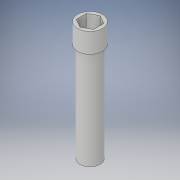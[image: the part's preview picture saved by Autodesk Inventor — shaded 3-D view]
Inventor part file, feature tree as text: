
AUTODESK INVENTOR PART (.ipt)
format: ipt  version: 2018 (Build 220112000, 112)  size: 112,640 bytes
history: native  units: in
note: dims shown in document units (in); Inventor stores cm internally (conversion verified against a paired STEP export)
features: extrude x3, sketch x3
ambient origin geometry x8: Origin, YZ Plane, XZ Plane, XY Plane, X Axis, Y Axis, Z Axis, Center Point
bodies: Solid1 (feature_tree)
feature tree (6):
  extrude  "Extrusion1"  Depth=1.0in TaperAngle=0.0deg
  extrude  "Extrusion2"  Depth=0.2in TaperAngle=0.0deg
  extrude  "Extrusion3"  [1 undecoded]
  sketch  "Sketch1"  dims[d0=0.2031in d1=1.0in d2=0.0in]
  sketch  "Sketch2"  dims[d3=0.25in d4=0.2in d5=0.0in]
  sketch  "Sketch3"  dims[d6=0.15in d7=0.0in]
note: 1 required parameter value undecoded (feature->parameter linkage not recoverable at this tier; creation-order binding heuristic only, values carry confidence <= 0.55)
